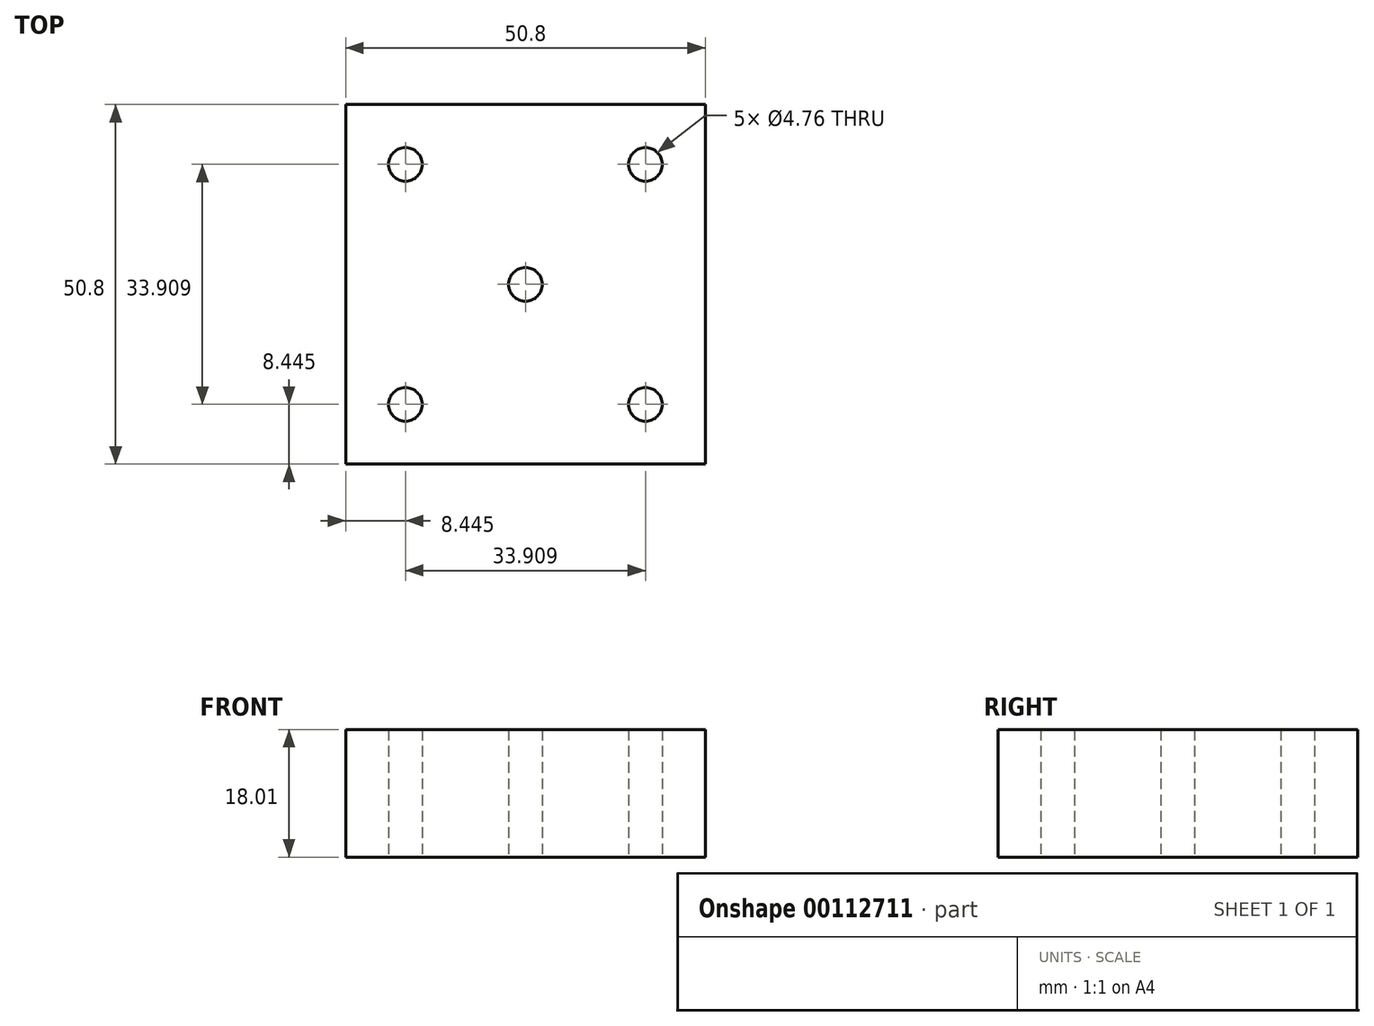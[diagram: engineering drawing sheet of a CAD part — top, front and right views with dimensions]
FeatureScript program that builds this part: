
annotation { "Feature Type Name" : "Feature", "Feature Type Description" : "" }
export const myFeature = defineFeature(function(context is Context, id is Id, definition is map)
    precondition{}
    {
        {
            var Q0;
            Q0=qCreatedBy(makeId("Top.planeOp"),FACE);
            var sketch = newSketch(context, id + "F0", { "sketchPlane" : qUnion([Q0])});
            skCircle(sketch, "E0", {"center": v(0, 0) * mm, "radius": 2.38 * mm});
            skLineSegment(sketch, "E1.bottom", {"start": v(25.4, -25.4) * mm, "end": v(-25.4, -25.4) * mm});
            skLineSegment(sketch, "E1.top", {"start": v(25.4, 25.4) * mm, "end": v(-25.4, 25.4) * mm});
            skLineSegment(sketch, "E1.left", {"start": v(25.4, -25.4) * mm, "end": v(25.4, 25.4) * mm});
            skLineSegment(sketch, "E1.right", {"start": v(-25.4, -25.4) * mm, "end": v(-25.4, 25.4) * mm});
            skLineSegment(sketch, "E2.bottom", {"start": v(16.95, 16.95) * mm, "end": v(-16.95, 16.95) * mm, "construction": true});
            skLineSegment(sketch, "E2.top", {"start": v(16.95, -16.95) * mm, "end": v(-16.95, -16.95) * mm, "construction": true});
            skLineSegment(sketch, "E2.left", {"start": v(16.95, 16.95) * mm, "end": v(16.95, -16.95) * mm, "construction": true});
            skLineSegment(sketch, "E2.right", {"start": v(-16.95, 16.95) * mm, "end": v(-16.95, -16.95) * mm, "construction": true});
            skCircle(sketch, "E3", {"center": v(0, 0) * mm, "radius": 14.4 * mm, "construction": true});
            skCircle(sketch, "E4", {"center": v(-16.95, 16.95) * mm, "radius": 2.38 * mm});
            skCircle(sketch, "E5", {"center": v(16.95, 16.95) * mm, "radius": 2.38 * mm});
            skCircle(sketch, "E6", {"center": v(-16.95, -16.95) * mm, "radius": 2.38 * mm});
            skCircle(sketch, "E7", {"center": v(16.95, -16.95) * mm, "radius": 2.38 * mm});
            skSolve(sketch);
        }
        {
            var Q0;
            Q0 = qSketchRegion(id + "F0", true);
            extrude(context, id + "F1", {"entities" : qUnion([Q0]), "depth" : 18 * mm});
        }
    });
